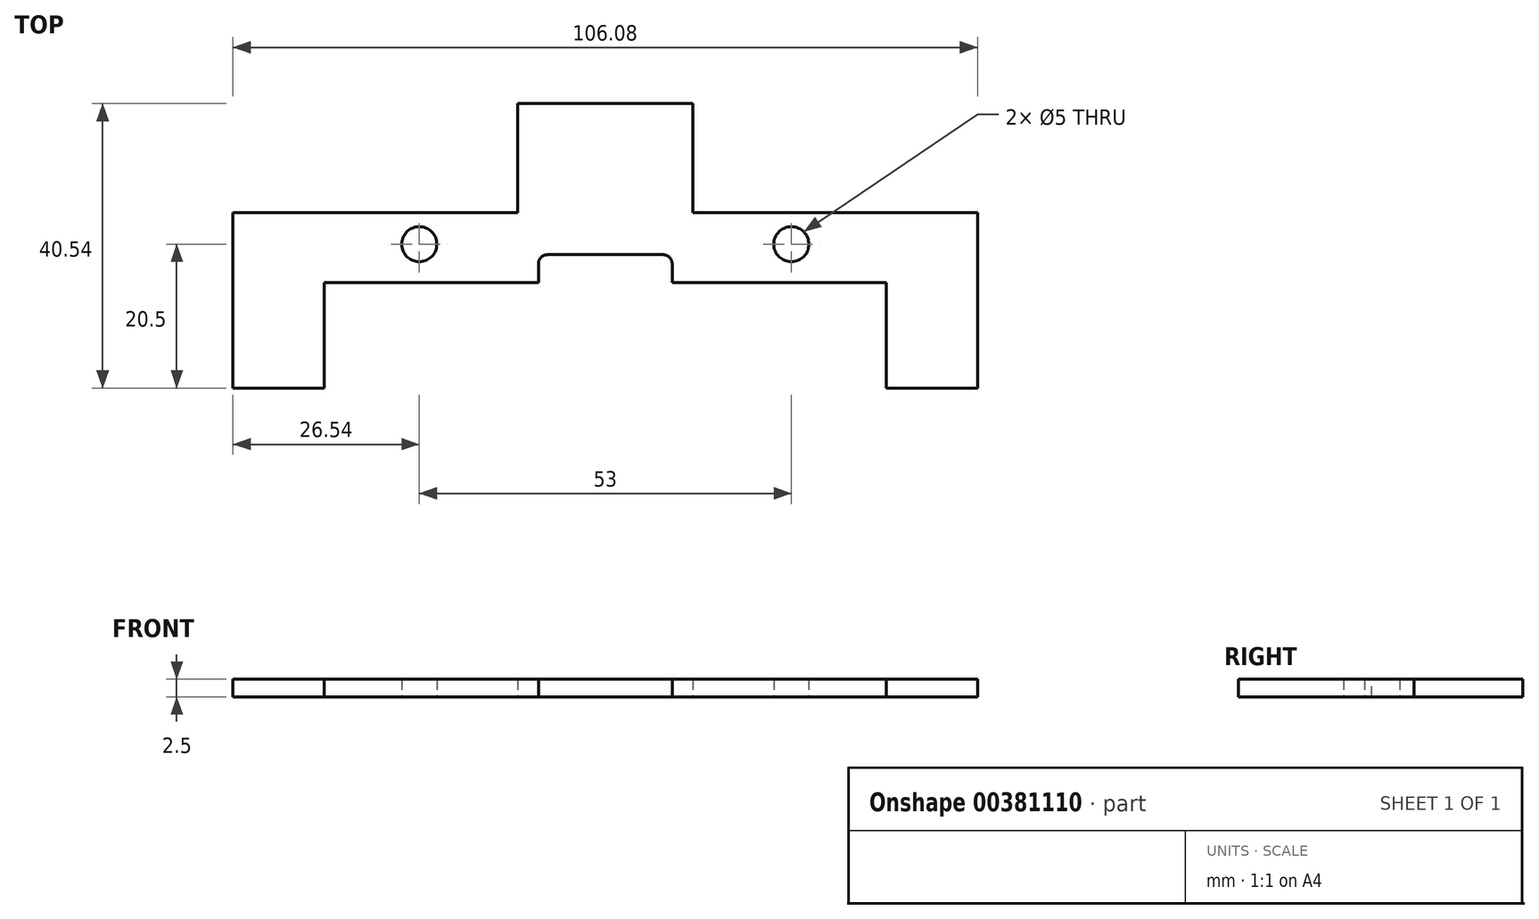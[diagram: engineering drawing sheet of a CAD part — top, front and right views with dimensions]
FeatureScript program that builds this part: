
annotation { "Feature Type Name" : "Feature", "Feature Type Description" : "" }
export const myFeature = defineFeature(function(context is Context, id is Id, definition is map)
    precondition{}
    {
        {
            var Q0;
            Q0=qCreatedBy(makeId("Top.planeOp"),FACE);
            var sketch = newSketch(context, id + "F0", { "sketchPlane" : qUnion([Q0])});
            skCircle(sketch, "E0", {"center": v(0, 0) * mm, "radius": 2.5 * mm});
            skCircle(sketch, "E1", {"center": v(53, 0) * mm, "radius": 2.5 * mm});
            skLineSegment(sketch, "E2.bottom", {"start": v(-4.5, 4.5) * mm, "end": v(57.5, 4.5) * mm});
            skLineSegment(sketch, "E2.top", {"start": v(-4.5, -5.5) * mm, "end": v(57.5, -5.5) * mm});
            skLineSegment(sketch, "E2.left", {"start": v(-4.5, 4.5) * mm, "end": v(-4.5, -5.5) * mm});
            skLineSegment(sketch, "E2.right", {"start": v(57.5, 4.5) * mm, "end": v(57.5, -5.5) * mm});
            skSolve(sketch);
        }
        {
            var Q0;
            Q0 = qSketchRegion(id + "F0", true);
            extrude(context, id + "F1", {"entities" : qUnion([Q0]), "depth" : 2.5 * mm});
        }
        {
            var Q0;
            Q0=makeQuery(id+"F1.opExtrude","CAP_FACE",FACE,{"disambiguationData":[OSD([sQuery(id+"F0.wireOp",EDGE,"E0"),sQuery(id+"F0.wireOp",EDGE,"E1"),sQuery(id+"F0.wireOp",EDGE,"E2.bottom"),sQuery(id+"F0.wireOp",EDGE,"E2.top"),sQuery(id+"F0.wireOp",EDGE,"E2.left"),sQuery(id+"F0.wireOp",EDGE,"E2.right")])],"isStart":false});
            var sketch = newSketch(context, id + "F2", { "sketchPlane" : qUnion([Q0])});
            skLineSegment(sketch, "E3.bottom", {"start": v(36.03, -5.5) * mm, "end": v(16.98, -5.5) * mm});
            skLineSegment(sketch, "E3.top", {"start": v(36.03, -1.5) * mm, "end": v(16.98, -1.5) * mm});
            skLineSegment(sketch, "E3.left", {"start": v(36.03, -5.5) * mm, "end": v(36.03, -1.5) * mm});
            skLineSegment(sketch, "E3.right", {"start": v(16.98, -5.5) * mm, "end": v(16.98, -1.5) * mm});
            skSolve(sketch);
        }
        {
            var Q0;
            Q0 = qSketchRegion(id + "F2", true);
            extrude(context, id + "F3", {"entities" : qUnion([Q0]), "operationType" : NewBodyOperationType.REMOVE, "oppositeDirection" : true, "depth" : 25.4 * mm});
        }
        {
            var Q0;
            Q0=makeQuery(id+"F3.boolean.opBoolean","COPY",EDGE,{"derivedFrom":makeQuery(id+"F3.opExtrude","SWEPT_EDGE",EDGE,{"disambiguationData":[OSD([sQuery(id+"F2.wireOp",EDGE,"E3.top"),sQuery(id+"F2.wireOp",EDGE,"E3.left")])]})});
            var Q1;
            Q1=makeQuery(id+"F3.boolean.opBoolean","COPY",EDGE,{"derivedFrom":makeQuery(id+"F3.opExtrude","SWEPT_EDGE",EDGE,{"disambiguationData":[OSD([sQuery(id+"F2.wireOp",EDGE,"E3.top"),sQuery(id+"F2.wireOp",EDGE,"E3.right")])]})});
            fillet(context, id + "F4", {"entities" : qUnion([Q0, Q1]), "radius" : 1.27 * mm, "tangentPropagation" : true, "allowEdgeOverflow" : false});
        }
        {
            var Q0;
            Q0=makeQuery(id+"F1.opExtrude","SWEPT_FACE",FACE,{"disambiguationData":[OSD([sQuery(id+"F0.wireOp",EDGE,"E2.bottom")])]});
            var sketch = newSketch(context, id + "F5", { "sketchPlane" : qUnion([Q0])});
            skLineSegment(sketch, "E4.bottom", {"start": v(-39, 2.5) * mm, "end": v(-14, 2.5) * mm});
            skLineSegment(sketch, "E4.top", {"start": v(-39, 0) * mm, "end": v(-14, 0) * mm});
            skLineSegment(sketch, "E4.left", {"start": v(-39, 2.5) * mm, "end": v(-39, 0) * mm});
            skLineSegment(sketch, "E4.right", {"start": v(-14, 2.5) * mm, "end": v(-14, 0) * mm});
            skSolve(sketch);
        }
        {
            var Q0;
            Q0=makeQuery(id+"F5.imprint","IMPRINT",FACE,{"disambiguationData":[TD([[makeQuery(id+"F5.imprint","IMPRINT",EDGE,{"derivedFrom":sQuery(id+"F5.wireOp",EDGE,"E4.bottom")}),1.0]])]});
            extrude(context, id + "F6", {"entities" : qUnion([Q0]), "operationType" : NewBodyOperationType.ADD, "depth" : 15.54 * mm});
        }
        {
            var Q0;
            Q0=makeQuery(id+"F1.opExtrude","SWEPT_FACE",FACE,{"disambiguationData":[OSD([sQuery(id+"F0.wireOp",EDGE,"E2.right")])]});
            extrude(context, id + "F7", {"entities" : qUnion([Q0]), "operationType" : NewBodyOperationType.ADD, "depth" : 22.04 * mm});
        }
        {
            var Q0;
            {var subQ0=sQuery(id+"F0.wireOp",EDGE,"E2.right");var subQ1=sQuery(id+"F0.wireOp",EDGE,"E2.top");Q0=makeQuery(id+"F7.boolean.opBoolean","MERGE",FACE,{"derivedFrom":[makeQuery(id+"F3.boolean.opBoolean","SPLIT",FACE,{"disambiguationData":[TD([makeQuery(id+"F1.opExtrude","SWEPT_FACE",FACE,{"disambiguationData":[OSD([subQ0])]})])],"derivedFrom":makeQuery(id+"F1.opExtrude","SWEPT_FACE",FACE,{"disambiguationData":[OSD([subQ1])]})}),makeQuery(id+"F7.opExtrude","SWEPT_FACE",FACE,{"disambiguationData":[OSD([subQ1,subQ0])]})]});}
            var sketch = newSketch(context, id + "F8", { "sketchPlane" : qUnion([Q0])});
            skLineSegment(sketch, "E5.bottom", {"start": v(79.54, 2.5) * mm, "end": v(66.54, 2.5) * mm});
            skLineSegment(sketch, "E5.top", {"start": v(79.54, 0) * mm, "end": v(66.54, 0) * mm});
            skLineSegment(sketch, "E5.left", {"start": v(79.54, 2.5) * mm, "end": v(79.54, 0) * mm});
            skLineSegment(sketch, "E5.right", {"start": v(66.54, 2.5) * mm, "end": v(66.54, 0) * mm});
            skSolve(sketch);
        }
        {
            var Q0;
            Q0 = qSketchRegion(id + "F8", true);
            extrude(context, id + "F9", {"entities" : qUnion([Q0]), "operationType" : NewBodyOperationType.ADD, "depth" : 35 * mm});
        }
        {
            var Q0;
            {var subQ0=sQuery(id+"F0.wireOp",EDGE,"E2.right");Q0=makeQuery(id+"F9.boolean.opBoolean","MERGE",FACE,{"derivedFrom":[makeQuery(id+"F7.boolean.opBoolean","MERGE",FACE,{"derivedFrom":[makeQuery(id+"F6.boolean.opBoolean","MERGE",FACE,{"derivedFrom":[makeQuery(id+"F1.opExtrude","CAP_FACE",FACE,{"disambiguationData":[OSD([sQuery(id+"F0.wireOp",EDGE,"E0"),sQuery(id+"F0.wireOp",EDGE,"E1"),sQuery(id+"F0.wireOp",EDGE,"E2.bottom"),sQuery(id+"F0.wireOp",EDGE,"E2.top"),sQuery(id+"F0.wireOp",EDGE,"E2.left"),subQ0])],"isStart":false}),makeQuery(id+"F6.opExtrude","SWEPT_FACE",FACE,{"disambiguationData":[OSD([sQuery(id+"F5.wireOp",EDGE,"E4.bottom")])]})]}),makeQuery(id+"F7.opExtrude","SWEPT_FACE",FACE,{"disambiguationData":[OSD([subQ0]),TDD([makeQuery(id+"F1.opExtrude","CAP_EDGE",EDGE,{"disambiguationData":[OSD([subQ0])],"isStart":false})])]})]}),makeQuery(id+"F9.opExtrude","SWEPT_FACE",FACE,{"disambiguationData":[OSD([sQuery(id+"F8.wireOp",EDGE,"E5.bottom")])]})]});}
            var sketch = newSketch(context, id + "F10", { "sketchPlane" : qUnion([Q0])});
            skLineSegment(sketch, "E6.bottom", {"start": v(79.54, 4.5) * mm, "end": v(72.04, 4.5) * mm});
            skLineSegment(sketch, "E6.top", {"start": v(79.54, -20.5) * mm, "end": v(72.04, -20.5) * mm});
            skLineSegment(sketch, "E6.left", {"start": v(79.54, 4.5) * mm, "end": v(79.54, -20.5) * mm});
            skLineSegment(sketch, "E6.right", {"start": v(72.04, 4.5) * mm, "end": v(72.04, -20.5) * mm});
            skSolve(sketch);
        }
        {
            var Q0;
            Q0=makeQuery(id+"F1.opExtrude","SWEPT_FACE",FACE,{"disambiguationData":[OSD([sQuery(id+"F0.wireOp",EDGE,"E2.left")])]});
            extrude(context, id + "F11", {"entities" : qUnion([Q0]), "operationType" : NewBodyOperationType.ADD, "depth" : 22.04 * mm});
        }
        {
            var Q0;
            {var subQ0=sQuery(id+"F0.wireOp",EDGE,"E2.left");var subQ1=sQuery(id+"F0.wireOp",EDGE,"E2.top");Q0=makeQuery(id+"F11.boolean.opBoolean","MERGE",FACE,{"derivedFrom":[makeQuery(id+"F3.boolean.opBoolean","SPLIT",FACE,{"disambiguationData":[TD([makeQuery(id+"F1.opExtrude","SWEPT_FACE",FACE,{"disambiguationData":[OSD([subQ0])]})])],"derivedFrom":makeQuery(id+"F1.opExtrude","SWEPT_FACE",FACE,{"disambiguationData":[OSD([subQ1])]})}),makeQuery(id+"F11.opExtrude","SWEPT_FACE",FACE,{"disambiguationData":[OSD([subQ1,subQ0])]})]});}
            var sketch = newSketch(context, id + "F12", { "sketchPlane" : qUnion([Q0])});
            skLineSegment(sketch, "E7.bottom", {"start": v(-26.54, 0) * mm, "end": v(-13.54, 0) * mm});
            skLineSegment(sketch, "E7.top", {"start": v(-26.54, 2.5) * mm, "end": v(-13.54, 2.5) * mm});
            skLineSegment(sketch, "E7.left", {"start": v(-26.54, 0) * mm, "end": v(-26.54, 2.5) * mm});
            skLineSegment(sketch, "E7.right", {"start": v(-13.54, 0) * mm, "end": v(-13.54, 2.5) * mm});
            skSolve(sketch);
        }
        {
            var Q0;
            Q0=makeQuery(id+"F12.imprint","IMPRINT",FACE,{"disambiguationData":[TD([[makeQuery(id+"F12.imprint","IMPRINT",EDGE,{"derivedFrom":sQuery(id+"F12.wireOp",EDGE,"E7.bottom")}),1.0]])]});
            extrude(context, id + "F13", {"entities" : qUnion([Q0]), "operationType" : NewBodyOperationType.ADD, "depth" : 35 * mm});
        }
        {
            var Q0;
            {var subQ0=sQuery(id+"F0.wireOp",EDGE,"E2.left");var subQ1=sQuery(id+"F0.wireOp",EDGE,"E2.right");Q0=makeQuery(id+"F13.boolean.opBoolean","MERGE",FACE,{"derivedFrom":[makeQuery(id+"F11.boolean.opBoolean","MERGE",FACE,{"derivedFrom":[makeQuery(id+"F9.boolean.opBoolean","MERGE",FACE,{"derivedFrom":[makeQuery(id+"F7.boolean.opBoolean","MERGE",FACE,{"derivedFrom":[makeQuery(id+"F6.boolean.opBoolean","MERGE",FACE,{"derivedFrom":[makeQuery(id+"F1.opExtrude","CAP_FACE",FACE,{"disambiguationData":[OSD([sQuery(id+"F0.wireOp",EDGE,"E0"),sQuery(id+"F0.wireOp",EDGE,"E1"),sQuery(id+"F0.wireOp",EDGE,"E2.bottom"),sQuery(id+"F0.wireOp",EDGE,"E2.top"),subQ0,subQ1])],"isStart":false}),makeQuery(id+"F6.opExtrude","SWEPT_FACE",FACE,{"disambiguationData":[OSD([sQuery(id+"F5.wireOp",EDGE,"E4.bottom")])]})]}),makeQuery(id+"F7.opExtrude","SWEPT_FACE",FACE,{"disambiguationData":[OSD([subQ1]),TDD([makeQuery(id+"F1.opExtrude","CAP_EDGE",EDGE,{"disambiguationData":[OSD([subQ1])],"isStart":false})])]})]}),makeQuery(id+"F9.opExtrude","SWEPT_FACE",FACE,{"disambiguationData":[OSD([sQuery(id+"F8.wireOp",EDGE,"E5.bottom")])]})]}),makeQuery(id+"F11.opExtrude","SWEPT_FACE",FACE,{"disambiguationData":[OSD([subQ0]),TDD([makeQuery(id+"F1.opExtrude","CAP_EDGE",EDGE,{"disambiguationData":[OSD([subQ0])],"isStart":false})])]})]}),makeQuery(id+"F13.opExtrude","SWEPT_FACE",FACE,{"disambiguationData":[OSD([sQuery(id+"F12.wireOp",EDGE,"E7.top")])]})]});}
            var sketch = newSketch(context, id + "F14", { "sketchPlane" : qUnion([Q0])});
            skLineSegment(sketch, "E8.bottom", {"start": v(-26.54, 4.5) * mm, "end": v(-19.04, 4.5) * mm});
            skLineSegment(sketch, "E8.top", {"start": v(-26.54, -20.5) * mm, "end": v(-19.04, -20.5) * mm});
            skLineSegment(sketch, "E8.left", {"start": v(-26.54, 4.5) * mm, "end": v(-26.54, -20.5) * mm});
            skLineSegment(sketch, "E8.right", {"start": v(-19.04, 4.5) * mm, "end": v(-19.04, -20.5) * mm});
            skSolve(sketch);
        }
        {
            var Q0;
            {var subQ14=sQuery(id+"F14.wireOp",EDGE,"E8.top");Q0=makeQuery(id+"F14.imprint","IMPRINT",FACE,{"disambiguationData":[TD([[makeQuery(id+"F14.imprint","IMPRINT",EDGE,{"derivedFrom":subQ14}),-1.0]])]});}
            var sketch = newSketch(context, id + "F15", { "sketchPlane" : qUnion([Q0])});
            skLineSegment(sketch, "E9.bottom", {"start": v(-26.54, -20.5) * mm, "end": v(79.54, -20.5) * mm});
            skLineSegment(sketch, "E9.top", {"start": v(-26.54, -58.45) * mm, "end": v(79.54, -58.45) * mm});
            skLineSegment(sketch, "E9.left", {"start": v(-26.54, -20.5) * mm, "end": v(-26.54, -58.45) * mm});
            skLineSegment(sketch, "E9.right", {"start": v(79.54, -20.5) * mm, "end": v(79.54, -58.45) * mm});
            skSolve(sketch);
        }
        {
            var Q0;
            Q0 = qSketchRegion(id + "F15", true);
            extrude(context, id + "F16", {"entities" : qUnion([Q0]), "operationType" : NewBodyOperationType.REMOVE, "endBound" : BoundingType.THROUGH_ALL, "oppositeDirection" : true, "depth" : 25.4 * mm});
        }
    });
